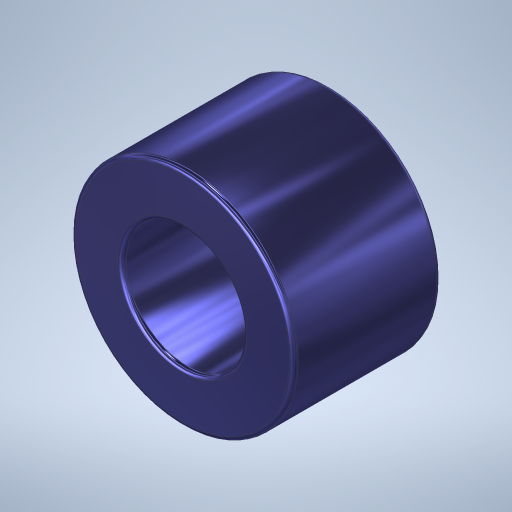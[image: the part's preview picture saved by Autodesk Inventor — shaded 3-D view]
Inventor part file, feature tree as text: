
AUTODESK INVENTOR PART (.ipt)
format: ipt  version: 2023.1 (Build 271208000, 208)  size: 305,152 bytes
history: native  units: in
note: dims shown in document units (in); Inventor stores cm internally (conversion verified against a paired STEP export)
features: extrude x1, fillet x1, sketch x1
ambient origin geometry x8: Origin, YZ Plane, XZ Plane, XY Plane, X Axis, Y Axis, Z Axis, Center Point
bodies: Solid1 (feature_tree)
feature tree (3):
  extrude  "Extrusion1"  Depth=0.005in
  fillet  "Fillet1"  Radius=0.165in
  sketch  "Sketch1"  dims[d0=0.25in d1=0.135in d2=0.165in d3=0.0in d4=0.005in]
